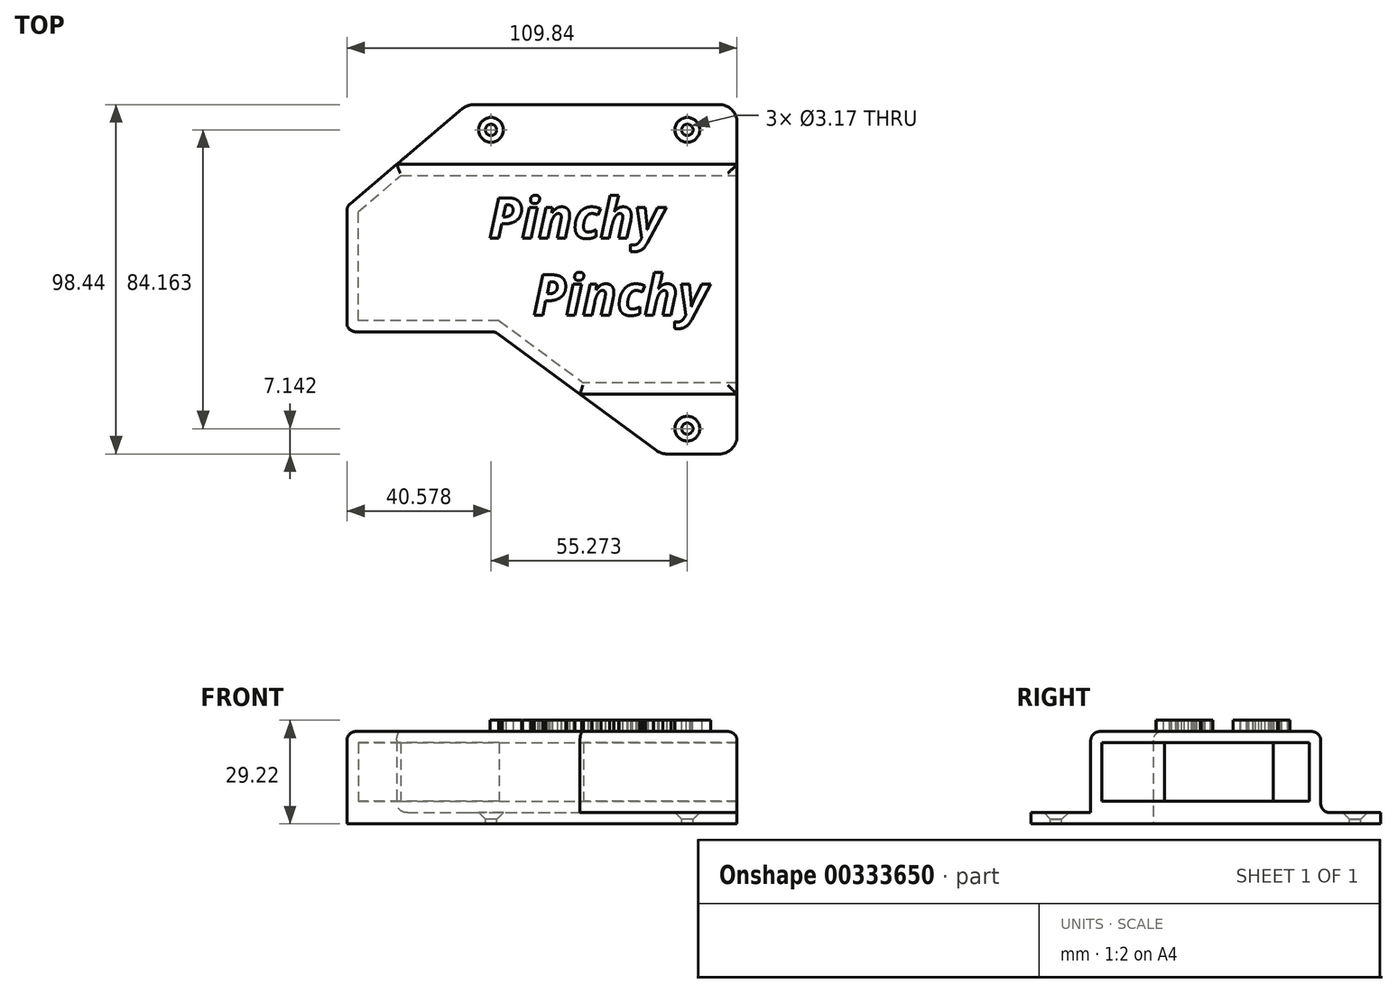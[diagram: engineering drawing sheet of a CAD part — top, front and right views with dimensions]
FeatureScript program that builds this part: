
annotation { "Feature Type Name" : "Feature", "Feature Type Description" : "" }
export const myFeature = defineFeature(function(context is Context, id is Id, definition is map)
    precondition{}
    {
        {
            var Q0;
            Q0=qCreatedBy(makeId("Top.planeOp"),FACE);
            var sketch = newSketch(context, id + "F0", { "sketchPlane" : qUnion([Q0])});
            skLineSegment(sketch, "E0.0", {"start": v(-37.29, -3.17) * mm, "end": v(-79.05, -3.18) * mm});
            skLineSegment(sketch, "E0.1", {"start": v(-37.29, -3.17) * mm, "end": v(-13.43, -20.74) * mm});
            skLineSegment(sketch, "E0.2", {"start": v(-79.05, 32.13) * mm, "end": v(-65, 44.03) * mm});
            skLineSegment(sketch, "E0.3", {"start": v(-65, 44.03) * mm, "end": v(30.79, 44.03) * mm});
            skLineSegment(sketch, "E0.4", {"start": v(30.79, 44.03) * mm, "end": v(30.79, -20.74) * mm});
            skLineSegment(sketch, "E0.5", {"start": v(-79.05, -3.18) * mm, "end": v(-79.05, 32.13) * mm});
            skLineSegment(sketch, "E0.6", {"start": v(30.79, -20.74) * mm, "end": v(-13.43, -20.74) * mm});
            skSolve(sketch);
        }
        {
            var Q0;
            Q0 = qSketchRegion(id + "F0", true);
            extrude(context, id + "F1", {"entities" : qUnion([Q0]), "depth" : 22.86 * mm});
        }
        {
            var Q0;
            Q0=makeQuery(id+"F1.opExtrude","SWEPT_FACE",FACE,{"disambiguationData":[OSD([sQuery(id+"F0.wireOp",EDGE,"E0.4")])]});
            shell(context, id + "F2", {"entities" : qUnion([Q0]), "thickness" : 3.17 * mm});
        }
        {
            var Q0;
            Q0=makeQuery(id+"F1.opExtrude","CAP_FACE",FACE,{"disambiguationData":[OSD([sQuery(id+"F0.wireOp",EDGE,"E0.0"),sQuery(id+"F0.wireOp",EDGE,"E0.1"),sQuery(id+"F0.wireOp",EDGE,"E0.2"),sQuery(id+"F0.wireOp",EDGE,"E0.3"),sQuery(id+"F0.wireOp",EDGE,"E0.4"),sQuery(id+"F0.wireOp",EDGE,"E0.5"),sQuery(id+"F0.wireOp",EDGE,"E0.6")])],"isStart":true});
            var sketch = newSketch(context, id + "F3", { "sketchPlane" : qUnion([Q0])});
            skLineSegment(sketch, "E1", {"start": v(-79.05, -32.13) * mm, "end": v(-45.13, -60.86) * mm});
            skLineSegment(sketch, "E2", {"start": v(-45.13, -60.86) * mm, "end": v(30.79, -60.86) * mm});
            skLineSegment(sketch, "E3", {"start": v(30.79, -60.86) * mm, "end": v(30.79, 37.58) * mm});
            skLineSegment(sketch, "E4", {"start": v(-79.05, -32.13) * mm, "end": v(-79.05, 3.18) * mm});
            skLineSegment(sketch, "E5", {"start": v(-79.05, 3.18) * mm, "end": v(-37.29, 3.17) * mm});
            skLineSegment(sketch, "E6", {"start": v(-37.29, 3.17) * mm, "end": v(-13.43, 20.74) * mm});
            skLineSegment(sketch, "E7", {"start": v(-13.43, 20.74) * mm, "end": v(9.45, 37.58) * mm});
            skLineSegment(sketch, "E8", {"start": v(9.45, 37.58) * mm, "end": v(30.79, 37.58) * mm});
            skSolve(sketch);
        }
        {
            var Q0;
            Q0 = qSketchRegion(id + "F3", true);
            extrude(context, id + "F4", {"entities" : qUnion([Q0]), "operationType" : NewBodyOperationType.ADD, "depth" : 3.17 * mm});
        }
        {
            var Q0;
            Q0=makeQuery(id+"F1.opExtrude","CAP_EDGE",EDGE,{"disambiguationData":[OSD([sQuery(id+"F0.wireOp",EDGE,"E0.3")])],"isStart":true});
            var Q1;
            Q1=makeQuery(id+"F1.opExtrude","CAP_EDGE",EDGE,{"disambiguationData":[OSD([sQuery(id+"F0.wireOp",EDGE,"E0.3")])],"isStart":false});
            var Q2;
            Q2=makeQuery(id+"F1.opExtrude","CAP_FACE",FACE,{"disambiguationData":[OSD([sQuery(id+"F0.wireOp",EDGE,"E0.0"),sQuery(id+"F0.wireOp",EDGE,"E0.1"),sQuery(id+"F0.wireOp",EDGE,"E0.2"),sQuery(id+"F0.wireOp",EDGE,"E0.3"),sQuery(id+"F0.wireOp",EDGE,"E0.4"),sQuery(id+"F0.wireOp",EDGE,"E0.5"),sQuery(id+"F0.wireOp",EDGE,"E0.6")])],"isStart":false});
            var Q3;
            Q3=makeQuery(id+"F1.opExtrude","CAP_EDGE",EDGE,{"disambiguationData":[OSD([sQuery(id+"F0.wireOp",EDGE,"E0.6")])],"isStart":true});
            var Q4;
            Q4=makeQuery(id+"F4.boolean.opBoolean","MERGE",EDGE,{"derivedFrom":[makeQuery(id+"F1.opExtrude","SWEPT_EDGE",EDGE,{"disambiguationData":[OSD([sQuery(id+"F0.wireOp",EDGE,"E0.0"),sQuery(id+"F0.wireOp",EDGE,"E0.5")])]}),makeQuery(id+"F4.opExtrude","SWEPT_EDGE",EDGE,{"disambiguationData":[OSD([sQuery(id+"F3.wireOp",EDGE,"E4"),sQuery(id+"F3.wireOp",EDGE,"E5")])]})]});
            var Q5;
            Q5=makeQuery(id+"F4.boolean.opBoolean","MERGE",EDGE,{"derivedFrom":[makeQuery(id+"F1.opExtrude","SWEPT_EDGE",EDGE,{"disambiguationData":[OSD([sQuery(id+"F0.wireOp",EDGE,"E0.2"),sQuery(id+"F0.wireOp",EDGE,"E0.5")])]}),makeQuery(id+"F4.opExtrude","SWEPT_EDGE",EDGE,{"disambiguationData":[OSD([sQuery(id+"F3.wireOp",EDGE,"E1"),sQuery(id+"F3.wireOp",EDGE,"E4")])]})]});
            var Q6;
            Q6=makeQuery(id+"F4.boolean.opBoolean","MERGE",EDGE,{"derivedFrom":[makeQuery(id+"F1.opExtrude","SWEPT_EDGE",EDGE,{"disambiguationData":[OSD([sQuery(id+"F0.wireOp",EDGE,"E0.0"),sQuery(id+"F0.wireOp",EDGE,"E0.1")])]}),makeQuery(id+"F4.opExtrude","SWEPT_EDGE",EDGE,{"disambiguationData":[OSD([sQuery(id+"F3.wireOp",EDGE,"E5"),sQuery(id+"F3.wireOp",EDGE,"E6")])]})]});
            fillet(context, id + "F5", {"entities" : qUnion([Q0, Q1, Q2, Q3, Q4, Q5, Q6]), "radius" : 2.54 * mm, "tangentPropagation" : true, "allowEdgeOverflow" : false});
        }
        {
            var Q0;
            Q0=makeQuery(id+"F1.opExtrude","CAP_FACE",FACE,{"disambiguationData":[OSD([sQuery(id+"F0.wireOp",EDGE,"E0.0"),sQuery(id+"F0.wireOp",EDGE,"E0.1"),sQuery(id+"F0.wireOp",EDGE,"E0.2"),sQuery(id+"F0.wireOp",EDGE,"E0.3"),sQuery(id+"F0.wireOp",EDGE,"E0.4"),sQuery(id+"F0.wireOp",EDGE,"E0.5"),sQuery(id+"F0.wireOp",EDGE,"E0.6")])],"isStart":false});
            var sketch = newSketch(context, id + "F6", { "sketchPlane" : qUnion([Q0])});
            skText(sketch, "E9", { "text": "Pinchy\n   Pinchy", "fontName": "OpenSans-BoldItalic.ttf"});
            const initialGuessF6  = {"E9": [-0.03912, 0.0232, 1, 0, 0.01148]};
            skSetInitialGuess(sketch, initialGuessF6);
            skSolve(sketch);
        }
        {
            var Q0;
            Q0 = qSketchRegion(id + "F6", true);
            extrude(context, id + "F7", {"entities" : qUnion([Q0]), "operationType" : NewBodyOperationType.ADD, "depth" : 3.17 * mm});
        }
        {
            var Q0;
            {var subQ0=sQuery(id+"F3.wireOp",EDGE,"E1");var subQ1=sQuery(id+"F3.wireOp",EDGE,"E2");var subQ2=sQuery(id+"F3.wireOp",EDGE,"E3");Q0=makeQuery(id+"F4.boolean.opBoolean","SPLIT",FACE,{"disambiguationData":[TD([makeQuery(id+"F1.opExtrude","SWEPT_FACE",FACE,{"disambiguationData":[OSD([sQuery(id+"F0.wireOp",EDGE,"E0.2")])]})])],"derivedFrom":makeQuery(id+"F4.opExtrude","CAP_FACE",FACE,{"disambiguationData":[OSD([subQ0,subQ1,subQ2,sQuery(id+"F3.wireOp",EDGE,"E4"),sQuery(id+"F3.wireOp",EDGE,"E5"),sQuery(id+"F3.wireOp",EDGE,"E6"),sQuery(id+"F3.wireOp",EDGE,"E7"),sQuery(id+"F3.wireOp",EDGE,"E8")])],"isStart":true})});}
            var sketch = newSketch(context, id + "F8", { "sketchPlane" : qUnion([Q0])});
            skPoint(sketch, "E10", {"position": v(-38.47, 53.72) * mm});
            skPoint(sketch, "E11", {"position": v(16.8, 53.72) * mm});
            skPoint(sketch, "E12", {"position": v(16.8, -30.44) * mm});
            skSolve(sketch);
        }
        {
            var Q0;
            Q0=makeQuery(id+"F4.opExtrude","SWEPT_EDGE",EDGE,{"disambiguationData":[OSD([sQuery(id+"F3.wireOp",EDGE,"E1"),sQuery(id+"F3.wireOp",EDGE,"E2")])]});
            var Q1;
            Q1=makeQuery(id+"F4.opExtrude","SWEPT_EDGE",EDGE,{"disambiguationData":[OSD([sQuery(id+"F3.wireOp",EDGE,"E2"),sQuery(id+"F3.wireOp",EDGE,"E3")])]});
            var Q2;
            Q2=makeQuery(id+"F4.opExtrude","SWEPT_EDGE",EDGE,{"disambiguationData":[OSD([sQuery(id+"F3.wireOp",EDGE,"E3"),sQuery(id+"F3.wireOp",EDGE,"E8")])]});
            var Q3;
            Q3=makeQuery(id+"F4.opExtrude","SWEPT_EDGE",EDGE,{"disambiguationData":[OSD([sQuery(id+"F3.wireOp",EDGE,"E7"),sQuery(id+"F3.wireOp",EDGE,"E8")])]});
            fillet(context, id + "F9", {"entities" : qUnion([Q0, Q1, Q2, Q3]), "radius" : 5.08 * mm, "tangentPropagation" : true, "allowEdgeOverflow" : false});
        }
        {
            var Q0;
            Q0=sQuery(id+"F8.wireOp",VERTEX,"E10");
            var Q1;
            Q1=sQuery(id+"F8.wireOp",VERTEX,"E11");
            var Q2;
            Q2=sQuery(id+"F8.wireOp",VERTEX,"E12");
            var Q3;
            Q3=makeQuery(id+"F1.opExtrude","SWEPT_BODY",BODY,{"disambiguationData":[OSD([sQuery(id+"F0.wireOp",EDGE,"E0.0"),sQuery(id+"F0.wireOp",EDGE,"E0.1"),sQuery(id+"F0.wireOp",EDGE,"E0.2"),sQuery(id+"F0.wireOp",EDGE,"E0.3"),sQuery(id+"F0.wireOp",EDGE,"E0.4"),sQuery(id+"F0.wireOp",EDGE,"E0.5"),sQuery(id+"F0.wireOp",EDGE,"E0.6")])]});
            hole(context, id + "F10", {"style" : HoleStyle.C_SINK, "endStyle" : HoleEndStyle.THROUGH, "holeDiameter" : 3.17 * mm, "cSinkDiameter" : 7 * mm, "cSinkAngle" : 90 * degree, "tappedDepth" : 12.7 * mm, "tapClearance" : 3, "locations" : qUnion([Q0, Q1, Q2]), "scope" : qUnion([Q3])});
        }
    });
